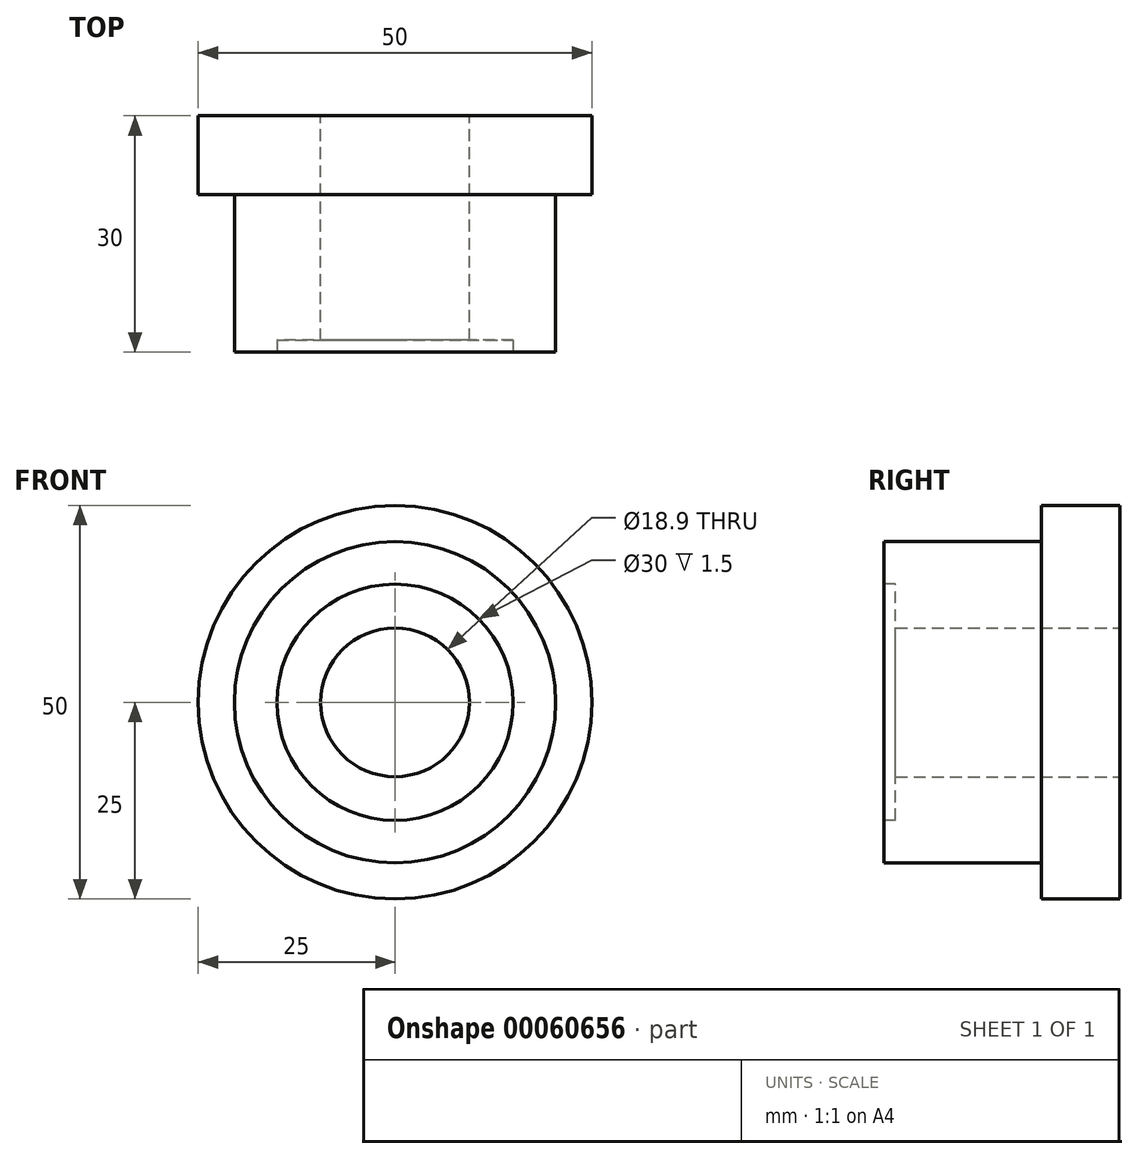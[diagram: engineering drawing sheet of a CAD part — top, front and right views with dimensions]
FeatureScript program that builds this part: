
annotation { "Feature Type Name" : "Feature", "Feature Type Description" : "" }
export const myFeature = defineFeature(function(context is Context, id is Id, definition is map)
    precondition{}
    {
        {
            var Q0;
            Q0=qCreatedBy(makeId("Front.planeOp"),FACE);
            var sketch = newSketch(context, id + "F0", { "sketchPlane" : qUnion([Q0])});
            skCircle(sketch, "E0", {"center": v(0, 0) * mm, "radius": 9.45 * mm});
            skCircle(sketch, "E1", {"center": v(0, 0) * mm, "radius": 25 * mm});
            skCircle(sketch, "E2", {"center": v(0, 0) * mm, "radius": 20.4 * mm});
            skSolve(sketch);
        }
        {
            var Q0;
            Q0=makeQuery(id+"F0.imprint","IMPRINT",FACE,{"disambiguationData":[TD([[makeQuery(id+"F0.imprint","IMPRINT",EDGE,{"derivedFrom":sQuery(id+"F0.wireOp",EDGE,"E0")}),-1.0]])]});
            extrude(context, id + "F1", {"entities" : qUnion([Q0]), "offsetDistance" : 25 * mm, "depth" : 30 * mm});
        }
        {
            var Q0;
            Q0=qSketchRegion(id+"F0",true);
            extrude(context, id + "F2", {"entities" : qUnion([Q0]), "operationType" : NewBodyOperationType.ADD, "offsetDistance" : 25 * mm, "depth" : 10 * mm});
        }
        {
            var Q0;
            Q0=makeQuery(id+"F1.opExtrude","CAP_FACE",FACE,{"disambiguationData":[OSD([sQuery(id+"F0.wireOp",EDGE,"E0"),sQuery(id+"F0.wireOp",EDGE,"E2")])],"isStart":false});
            var sketch = newSketch(context, id + "F3", { "sketchPlane" : qUnion([Q0])});
            skCircle(sketch, "E3", {"center": v(0, 0) * mm, "radius": 15 * mm});
            skSolve(sketch);
        }
        {
            var Q0;
            Q0=makeQuery(id+"F3.imprint","IMPRINT",FACE,{"disambiguationData":[TD([[makeQuery(id+"F3.imprint","IMPRINT",EDGE,{"derivedFrom":sQuery(id+"F3.wireOp",EDGE,"E3")}),1.0]])]});
            extrude(context, id + "F4", {"entities" : qUnion([Q0]), "operationType" : NewBodyOperationType.REMOVE, "oppositeDirection" : true, "offsetDistance" : 25 * mm, "depth" : 1.5 * mm});
        }
    });
